# Revit family: Drinking_Fountain-Oasis-Aqua_Pointe_Sports_Bottle_Filler-M8EBF
name_source: partatom
category: Plumbing Fixtures
revit_build: Autodesk Revit MEP 2013 (Build: 20130531_2115(x64)
units: mm (PartAtom-declared; Revit-internal decimal feet)

## types (2) — shared parameters
Apparent Load = 620 VA
Base Material = Metal - Oasis International - Brushed Stainless Steel - Exterior Finish
CW Connection = No
Chiller = Yes
Cold Water Connector = Cold Water Connection
Cold Water Diameter = 0"
Cold Water Radius = 0"
Compression HP = 0 VA
Default Elevation = 2' - 3"
Description = Aqua Pointe Sports Bottle Filler
Display Panel = Screen – Oasis- XXXX Display
Finish = Metal - Oasis International - Brushed Stainless Steel - Exterior Finish
Full Load Amps = 5 A
Manufacturer = Oasis International
Manufacturer Fax Number = (614)322-4557
Metal Finish = Metal - Oasis International - Brushed Stainless Steel - Exterior Finish
Number of Poles = 1
Power Factor = 1
Product Name = Radii Fountain w/ Electronic Bottle Filler
Sanitary Connector = Sanitary Connection
Sanitary Diameter = 0"
Sanitary Radius = 0"
URL = http://www.oasiscoolers.com
Voltage = 115 V
Waste Connection = No
Width = 3' - 2 3/4"
zero-valued in all types: CWFU, WFU

## per-type parameters (varying)
| type | Base Rate | Rated Capacity | Rated Watts |
| M8EBF | 8 GPM | 8 GPM | 550 W |
| M12EBF | 12 GPM | 12 GPM | 620 W |

note: column(s) folded — value = type name in every type: Model

## geometry (parser evidence)
native form markers: Blend x16, Sweep x27
no freeform markers — native parametric forms only
